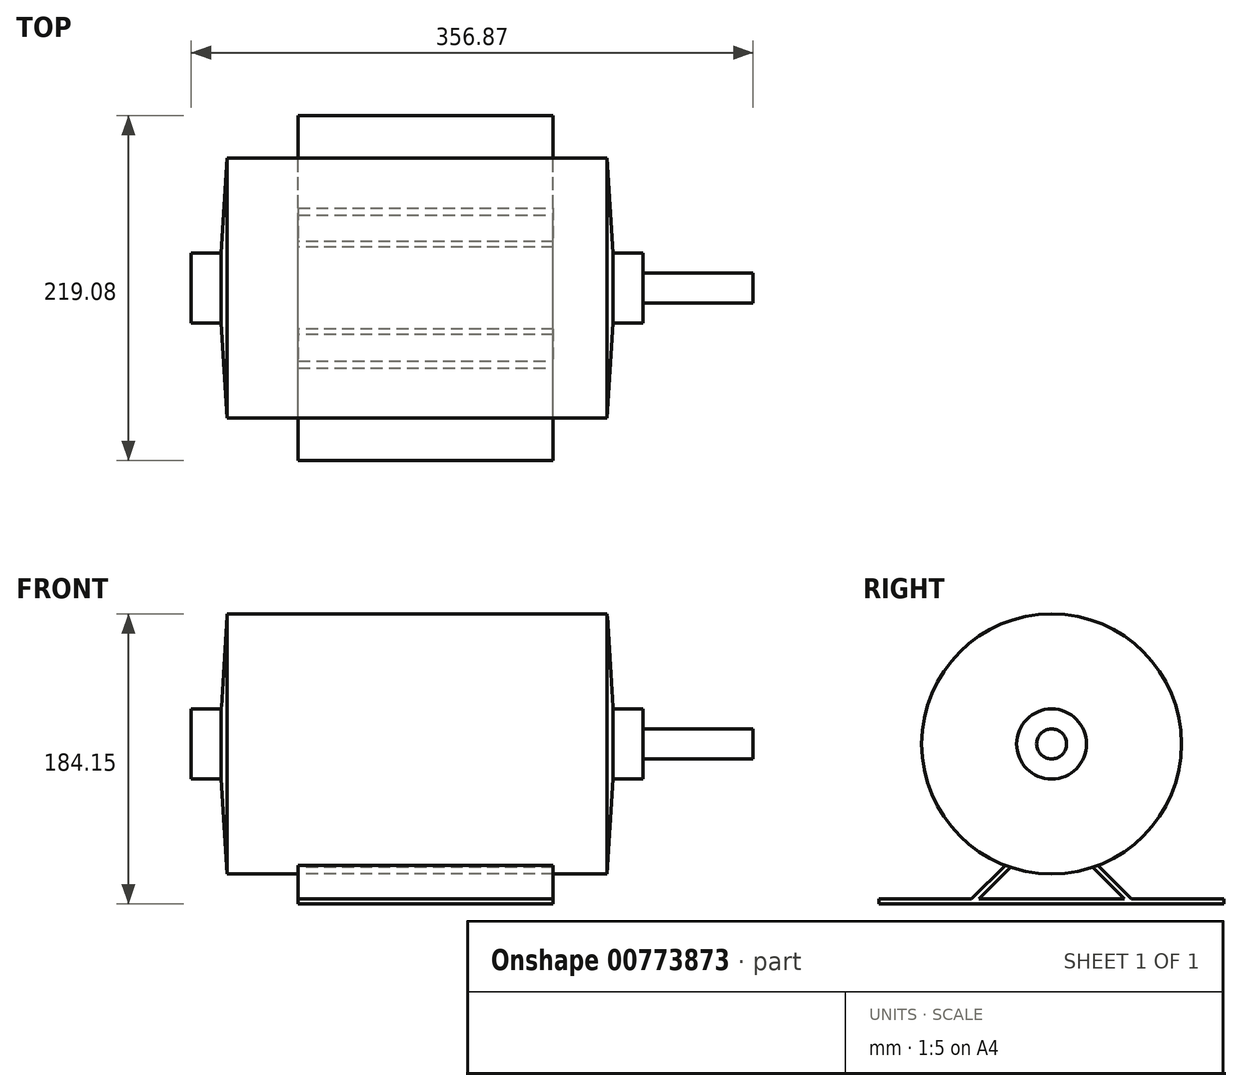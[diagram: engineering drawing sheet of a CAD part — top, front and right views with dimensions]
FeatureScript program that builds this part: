
annotation { "Feature Type Name" : "Feature", "Feature Type Description" : "" }
export const myFeature = defineFeature(function(context is Context, id is Id, definition is map)
    precondition{}
    {
        {
            var Q0;
            Q0=qCreatedBy(makeId("Top.planeOp"),FACE);
            var sketch = newSketch(context, id + "F0", { "sketchPlane" : qUnion([Q0])});
            skLineSegment(sketch, "E0", {"start": v(0, 0) * mm, "end": v(0, 22.23) * mm});
            skLineSegment(sketch, "E1", {"start": v(0, 22.23) * mm, "end": v(-19.05, 22.23) * mm});
            skLineSegment(sketch, "E2", {"start": v(-19.05, 22.23) * mm, "end": v(-22.86, 82.55) * mm});
            skLineSegment(sketch, "E3", {"start": v(-22.86, 82.55) * mm, "end": v(-264.16, 82.55) * mm});
            skLineSegment(sketch, "E4", {"start": v(-264.16, 82.55) * mm, "end": v(-267.97, 22.23) * mm});
            skLineSegment(sketch, "E5", {"start": v(-267.97, 22.22) * mm, "end": v(-287.02, 22.22) * mm});
            skLineSegment(sketch, "E6", {"start": v(-287.02, 22.22) * mm, "end": v(-287.02, 0) * mm});
            skLineSegment(sketch, "E7", {"start": v(-287.02, 0) * mm, "end": v(0, 0) * mm});
            skSolve(sketch);
        }
        {
            var Q0;
            Q0=makeQuery(id+"F0.imprint","IMPRINT",FACE,{"disambiguationData":[TD([[makeQuery(id+"F0.imprint","IMPRINT",EDGE,{"derivedFrom":sQuery(id+"F0.wireOp",EDGE,"E0")}),1.0]])]});
            var Q1;
            Q1=sQuery(id+"F0.wireOp",EDGE,"E7");
            revolve(context, id + "F1", {"surfaceOperationType" : NewSurfaceOperationType.NEW, "entities" : qUnion([Q0]), "axis" : qUnion([Q1]), "revolveType" : RevolveType.FULL});
        }
        {
            var Q0;
            Q0=makeQuery(id+"F1.opRevolve","SWEPT_FACE",FACE,{"disambiguationData":[OSD([sQuery(id+"F0.wireOp",EDGE,"E0")])]});
            var sketch = newSketch(context, id + "F2", { "sketchPlane" : qUnion([Q0])});
            skCircle(sketch, "E8", {"center": v(0, 0) * mm, "radius": 9.53 * mm});
            skSolve(sketch);
        }
        {
            var Q0;
            Q0 = qSketchRegion(id + "F2", true);
            extrude(context, id + "F3", {"entities" : qUnion([Q0]), "operationType" : NewBodyOperationType.ADD, "depth" : 69.85 * mm, "offsetDistance" : 25.4 * mm});
        }
        {
            var Q0;
            Q0=qCreatedBy(makeId("Right.planeOp"),FACE);
            cPlane(context, id + "F4", {"entities" : qUnion([Q0]), "cplaneType" : CPlaneType.OFFSET, "offset" : 57.15 * mm, "oppositeDirection" : true, "width" : 152.4 * mm, "height" : 152.4 * mm});
        }
        {
            var Q0;
            Q0=qCreatedBy(id+"F4.planeOp",FACE);
            var sketch = newSketch(context, id + "F5", { "sketchPlane" : qUnion([Q0])});
            skLineSegment(sketch, "E9.bottom", {"start": v(-109.54, -98.43) * mm, "end": v(-50.8, -98.43) * mm});
            skLineSegment(sketch, "E9.top", {"start": v(-109.54, -101.6) * mm, "end": v(109.54, -101.6) * mm});
            skLineSegment(sketch, "E9.left", {"start": v(-109.54, -98.43) * mm, "end": v(-109.54, -101.6) * mm});
            skLineSegment(sketch, "E9.right", {"start": v(109.54, -98.43) * mm, "end": v(109.54, -101.6) * mm});
            skLineSegment(sketch, "E10", {"start": v(-50.8, -98.42) * mm, "end": v(-14.88, -62.5) * mm});
            skLineSegment(sketch, "E11", {"start": v(-14.88, -62.5) * mm, "end": v(-12.63, -64.75) * mm});
            skLineSegment(sketch, "E12", {"start": v(-12.63, -64.75) * mm, "end": v(-46.3, -98.43) * mm});
            skLineSegment(sketch, "E13", {"start": v(50.8, -98.42) * mm, "end": v(14.88, -62.5) * mm});
            skLineSegment(sketch, "E14", {"start": v(14.88, -62.5) * mm, "end": v(12.63, -64.75) * mm});
            skLineSegment(sketch, "E15", {"start": v(12.63, -64.75) * mm, "end": v(46.3, -98.43) * mm});
            skLineSegment(sketch, "E16.trimOffspring", {"start": v(-46.3, -98.43) * mm, "end": v(46.3, -98.43) * mm});
            skLineSegment(sketch, "E17.trimOffspring", {"start": v(50.8, -98.43) * mm, "end": v(109.54, -98.43) * mm});
            skSolve(sketch);
        }
        {
            var Q0;
            Q0 = qSketchRegion(id + "F5", true);
            extrude(context, id + "F6", {"entities" : qUnion([Q0]), "operationType" : NewBodyOperationType.ADD, "oppositeDirection" : true, "depth" : 161.92 * mm, "offsetDistance" : 25.4 * mm});
        }
    });
